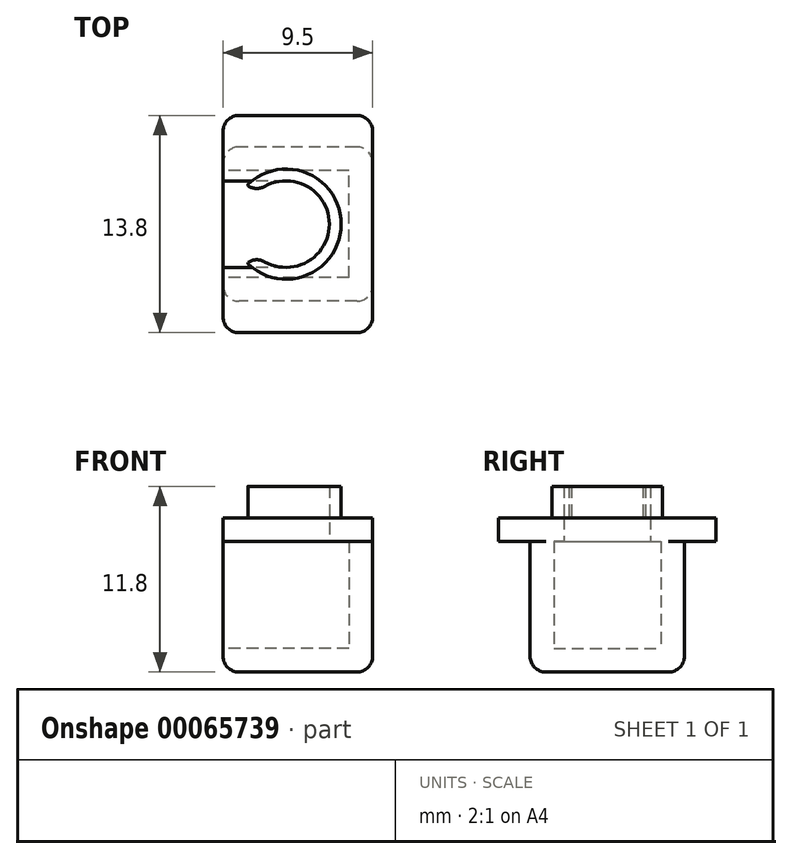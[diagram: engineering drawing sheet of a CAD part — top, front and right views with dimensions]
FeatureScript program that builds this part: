
annotation { "Feature Type Name" : "Feature", "Feature Type Description" : "" }
export const myFeature = defineFeature(function(context is Context, id is Id, definition is map)
    precondition{}
    {
        {
            var Q0;
            Q0=qCreatedBy(makeId("Top.planeOp"),FACE);
            var sketch = newSketch(context, id + "F0", { "sketchPlane" : qUnion([Q0])});
            skLineSegment(sketch, "E0.rect.bottom", {"start": v(4, -3.4) * mm, "end": v(-4, -3.4) * mm});
            skLineSegment(sketch, "E0.rect.top", {"start": v(4, 3.4) * mm, "end": v(-4, 3.4) * mm});
            skLineSegment(sketch, "E0.rect.left", {"start": v(4, -3.4) * mm, "end": v(4, 3.4) * mm});
            skLineSegment(sketch, "E0.rect.right", {"start": v(-4, -3.4) * mm, "end": v(-4, 3.4) * mm});
            skPoint(sketch, "E0.rect.middle", {"position": v(0, 0) * mm});
            skLineSegment(sketch, "E1.0", {"start": v(5.5, 4.9) * mm, "end": v(-4, 4.9) * mm});
            skLineSegment(sketch, "E1.1", {"start": v(5.5, -4.9) * mm, "end": v(5.5, 4.9) * mm});
            skLineSegment(sketch, "E1.2", {"start": v(5.5, -4.9) * mm, "end": v(-4, -4.9) * mm});
            skLineSegment(sketch, "E2", {"start": v(-4, 4.9) * mm, "end": v(-4, 3.4) * mm});
            skLineSegment(sketch, "E3", {"start": v(-4, -3.4) * mm, "end": v(-4, -4.9) * mm});
            skSolve(sketch);
        }
        {
            var Q0;
            Q0 = qSketchRegion(id + "F0", true);
            extrude(context, id + "F1", {"entities" : qUnion([Q0]), "oppositeDirection" : true, "depth" : 1.5 * mm});
        }
        {
            var Q0;
            Q0=makeQuery(id+"F0.imprint","IMPRINT",FACE,{"disambiguationData":[TD([[makeQuery(id+"F0.imprint","IMPRINT",EDGE,{"derivedFrom":sQuery(id+"F0.wireOp",EDGE,"E0.rect.bottom")}),1.0]])]});
            extrude(context, id + "F2", {"entities" : qUnion([Q0]), "operationType" : NewBodyOperationType.ADD, "depth" : 6.8 * mm});
        }
        {
            var Q0;
            Q0=makeQuery(id+"F2.opExtrude","CAP_FACE",FACE,{"disambiguationData":[OSD([sQuery(id+"F0.wireOp",EDGE,"E0.rect.bottom"),sQuery(id+"F0.wireOp",EDGE,"E0.rect.top"),sQuery(id+"F0.wireOp",EDGE,"E0.rect.left"),sQuery(id+"F0.wireOp",EDGE,"E1.0"),sQuery(id+"F0.wireOp",EDGE,"E1.1"),sQuery(id+"F0.wireOp",EDGE,"E1.2"),sQuery(id+"F0.wireOp",EDGE,"E2"),sQuery(id+"F0.wireOp",EDGE,"E3")])],"isStart":false});
            var sketch = newSketch(context, id + "F3", { "sketchPlane" : qUnion([Q0])});
            skArc(sketch, "E4", {"start": v(0, -2.75) * mm, "mid": v(2.75, 0) * mm, "end": v(0, 2.75) * mm});
            skLineSegment(sketch, "E5", {"start": v(0, 2.75) * mm, "end": v(-4, 2.75) * mm});
            skLineSegment(sketch, "E6", {"start": v(-4, 2.75) * mm, "end": v(-4, 4.9) * mm});
            skLineSegment(sketch, "E7", {"start": v(0, -2.75) * mm, "end": v(-4, -2.75) * mm});
            skLineSegment(sketch, "E8", {"start": v(-4, -2.75) * mm, "end": v(-4, -4.9) * mm});
            skSolve(sketch);
        }
        {
            var Q0;
            Q0=makeQuery(id+"F3.imprint","IMPRINT",FACE,{"disambiguationData":[TD([[makeQuery(id+"F3.imprint","IMPRINT",EDGE,{"derivedFrom":sQuery(id+"F3.wireOp",EDGE,"E4")}),-1.0]])]});
            var Q1;
            {var subQ4=makeQuery(id+"F2.opExtrude","CAP_EDGE",EDGE,{"disambiguationData":[OSD([sQuery(id+"F0.wireOp",EDGE,"E0.rect.bottom")])],"isStart":false});Q1=makeQuery(id+"F3.imprint","IMPRINT",FACE,{"disambiguationData":[TD([[makeQuery(id+"F3.imprint","IMPRINT",EDGE,{"derivedFrom":subQ4}),1.0]])]});}
            extrude(context, id + "F4", {"entities" : qUnion([Q0, Q1]), "operationType" : NewBodyOperationType.ADD, "depth" : 1.5 * mm});
        }
        {
            var Q0;
            Q0=makeQuery(id+"F4.opExtrude","CAP_FACE",FACE,{"disambiguationData":[OSD([sQuery(id+"F0.wireOp",EDGE,"E1.0"),sQuery(id+"F0.wireOp",EDGE,"E1.1"),sQuery(id+"F0.wireOp",EDGE,"E1.2"),sQuery(id+"F3.wireOp",EDGE,"E4"),sQuery(id+"F3.wireOp",EDGE,"E5"),sQuery(id+"F3.wireOp",EDGE,"E6"),sQuery(id+"F3.wireOp",EDGE,"E7"),sQuery(id+"F3.wireOp",EDGE,"E8")])],"isStart":false});
            var sketch = newSketch(context, id + "F5", { "sketchPlane" : qUnion([Q0])});
            skArc(sketch, "E9", {"start": v(-1.36, -2.4) * mm, "mid": v(2.75, 0) * mm, "end": v(-1.36, 2.4) * mm});
            skArc(sketch, "E10", {"start": v(-2.38, -2.57) * mm, "mid": v(3.5, 0) * mm, "end": v(-2.38, 2.57) * mm});
            skLineSegment(sketch, "E11", {"start": v(-2.38, 2.38) * mm, "end": v(-2.56, 2.56) * mm});
            skLineSegment(sketch, "E12.MirrorCS", {"start": v(-2.38, -2.38) * mm, "end": v(-2.56, -2.56) * mm});
            skPoint(sketch, "E13.visualSharp", {"position": v(-2.47, 2.47) * mm});
            skArc(sketch, "E13.filletArc", {"start": v(-2.38, 2.57) * mm, "mid": v(-2.42, 2.48) * mm, "end": v(-2.38, 2.38) * mm});
            skPoint(sketch, "E14.visualSharp", {"position": v(-2.47, -2.47) * mm});
            skArc(sketch, "E14.filletArc", {"start": v(-2.38, -2.38) * mm, "mid": v(-2.42, -2.48) * mm, "end": v(-2.38, -2.57) * mm});
            skPoint(sketch, "E15.visualSharp", {"position": v(-1.94, 1.94) * mm});
            skArc(sketch, "E15.filletArc", {"start": v(-2.56, 2.56) * mm, "mid": v(-1.98, 2.27) * mm, "end": v(-1.36, 2.4) * mm});
            skPoint(sketch, "E16.visualSharp", {"position": v(-1.94, -1.94) * mm});
            skArc(sketch, "E16.filletArc", {"start": v(-1.36, -2.4) * mm, "mid": v(-1.98, -2.27) * mm, "end": v(-2.56, -2.56) * mm});
            skSolve(sketch);
        }
        {
            var Q0;
            {var subQ0=sQuery(id+"F5.wireOp",EDGE,"E9");var subQ1=makeQuery(id+"F4.opExtrude","CAP_EDGE",EDGE,{"disambiguationData":[OSD([sQuery(id+"F3.wireOp",EDGE,"E7")])],"isStart":false});var subQ2=makeQuery(id+"F5.imprint","INTERSECT",VERTEX,{"derivedFrom":[subQ1,subQ0]});Q0=makeQuery(id+"F5.imprint","IMPRINT",FACE,{"disambiguationData":[TD([[makeQuery(id+"F5.imprint","IMPRINT",EDGE,{"disambiguationData":[TD([[subQ2,-1.0]])],"derivedFrom":subQ0}),-1.0]])]});}
            var Q1;
            {var subQ1=sQuery(id+"F5.wireOp",EDGE,"E9");var subQ7=makeQuery(id+"F4.opExtrude","CAP_EDGE",EDGE,{"disambiguationData":[OSD([sQuery(id+"F3.wireOp",EDGE,"E5")])],"isStart":false});var subQ9=makeQuery(id+"F5.imprint","INTERSECT",VERTEX,{"derivedFrom":[subQ7,subQ1]});Q1=makeQuery(id+"F5.imprint","IMPRINT",FACE,{"disambiguationData":[TD([[makeQuery(id+"F5.imprint","IMPRINT",EDGE,{"disambiguationData":[TD([[subQ9,-1.0]])],"derivedFrom":subQ1}),-1.0]])]});}
            var Q2;
            {var subQ1=sQuery(id+"F5.wireOp",EDGE,"E9");var subQ7=makeQuery(id+"F4.opExtrude","CAP_EDGE",EDGE,{"disambiguationData":[OSD([sQuery(id+"F3.wireOp",EDGE,"E7")])],"isStart":false});var subQ9=makeQuery(id+"F5.imprint","INTERSECT",VERTEX,{"derivedFrom":[subQ7,subQ1]});Q2=makeQuery(id+"F5.imprint","IMPRINT",FACE,{"disambiguationData":[TD([[makeQuery(id+"F5.imprint","IMPRINT",EDGE,{"disambiguationData":[TD([[subQ9,1.0]])],"derivedFrom":subQ1}),-1.0]])]});}
            extrude(context, id + "F6", {"entities" : qUnion([Q0, Q1, Q2]), "operationType" : NewBodyOperationType.ADD, "depth" : 2 * mm});
        }
        {
            var Q0;
            {var subQ0=sQuery(id+"F0.wireOp",EDGE,"E1.0");Q0=makeQuery(id+"F4.boolean.opBoolean","MERGE",FACE,{"derivedFrom":[makeQuery(id+"F2.boolean.opBoolean","MERGE",FACE,{"derivedFrom":[makeQuery(id+"F1.opExtrude","SWEPT_FACE",FACE,{"disambiguationData":[OSD([subQ0])]}),makeQuery(id+"F2.opExtrude","SWEPT_FACE",FACE,{"disambiguationData":[OSD([subQ0])]})]}),makeQuery(id+"F4.opExtrude","SWEPT_FACE",FACE,{"disambiguationData":[OSD([subQ0])]})]});}
            var sketch = newSketch(context, id + "F7", { "sketchPlane" : qUnion([Q0])});
            skLineSegment(sketch, "E17", {"start": v(-5.5, 6.8) * mm, "end": v(4, 6.8) * mm});
            skSolve(sketch);
        }
        {
            var Q0;
            {var subQ0=sQuery(id+"F7.wireOp",EDGE,"E17");Q0=makeQuery(id+"F7.imprint","IMPRINT",FACE,{"disambiguationData":[TD([[makeQuery(id+"F7.imprint","IMPRINT",EDGE,{"derivedFrom":subQ0}),1.0]])]});}
            extrude(context, id + "F8", {"entities" : qUnion([Q0]), "operationType" : NewBodyOperationType.ADD, "depth" : 2 * mm});
        }
        {
            var Q0;
            {var subQ0=sQuery(id+"F0.wireOp",EDGE,"E1.2");Q0=makeQuery(id+"F4.boolean.opBoolean","MERGE",FACE,{"derivedFrom":[makeQuery(id+"F2.boolean.opBoolean","MERGE",FACE,{"derivedFrom":[makeQuery(id+"F1.opExtrude","SWEPT_FACE",FACE,{"disambiguationData":[OSD([subQ0])]}),makeQuery(id+"F2.opExtrude","SWEPT_FACE",FACE,{"disambiguationData":[OSD([subQ0])]})]}),makeQuery(id+"F4.opExtrude","SWEPT_FACE",FACE,{"disambiguationData":[OSD([subQ0])]})]});}
            var sketch = newSketch(context, id + "F9", { "sketchPlane" : qUnion([Q0])});
            skLineSegment(sketch, "E18", {"start": v(5.5, 6.8) * mm, "end": v(-4, 6.8) * mm});
            skSolve(sketch);
        }
        {
            var Q0;
            {var subQ0=sQuery(id+"F9.wireOp",EDGE,"E18");Q0=makeQuery(id+"F9.imprint","IMPRINT",FACE,{"disambiguationData":[TD([[makeQuery(id+"F9.imprint","IMPRINT",EDGE,{"derivedFrom":subQ0}),-1.0]])]});}
            extrude(context, id + "F10", {"entities" : qUnion([Q0]), "operationType" : NewBodyOperationType.ADD, "depth" : 2 * mm});
        }
        {
            var Q0;
            Q0=makeQuery(id+"F1.opExtrude","CAP_EDGE",EDGE,{"disambiguationData":[OSD([sQuery(id+"F0.wireOp",EDGE,"E1.2")])],"isStart":false});
            var Q1;
            {var subQ0=sQuery(id+"F0.wireOp",EDGE,"E1.2");var subQ1=sQuery(id+"F0.wireOp",EDGE,"E1.1");Q1=makeQuery(id+"F4.boolean.opBoolean","MERGE",EDGE,{"derivedFrom":[makeQuery(id+"F2.boolean.opBoolean","MERGE",EDGE,{"derivedFrom":[makeQuery(id+"F1.opExtrude","SWEPT_EDGE",EDGE,{"disambiguationData":[OSD([subQ1,subQ0])]}),makeQuery(id+"F2.opExtrude","SWEPT_EDGE",EDGE,{"disambiguationData":[OSD([subQ1,subQ0])]})]}),makeQuery(id+"F4.opExtrude","SWEPT_EDGE",EDGE,{"disambiguationData":[OSD([subQ1,subQ0])]})]});}
            var Q2;
            {var subQ0=sQuery(id+"F0.wireOp",EDGE,"E1.1");var subQ1=sQuery(id+"F0.wireOp",EDGE,"E1.0");Q2=makeQuery(id+"F4.boolean.opBoolean","MERGE",EDGE,{"derivedFrom":[makeQuery(id+"F2.boolean.opBoolean","MERGE",EDGE,{"derivedFrom":[makeQuery(id+"F1.opExtrude","SWEPT_EDGE",EDGE,{"disambiguationData":[OSD([subQ1,subQ0])]}),makeQuery(id+"F2.opExtrude","SWEPT_EDGE",EDGE,{"disambiguationData":[OSD([subQ1,subQ0])]})]}),makeQuery(id+"F4.opExtrude","SWEPT_EDGE",EDGE,{"disambiguationData":[OSD([subQ1,subQ0])]})]});}
            var Q3;
            Q3=makeQuery(id+"F1.opExtrude","CAP_EDGE",EDGE,{"disambiguationData":[OSD([sQuery(id+"F0.wireOp",EDGE,"E1.1")])],"isStart":false});
            var Q4;
            Q4=makeQuery(id+"F1.opExtrude","CAP_EDGE",EDGE,{"disambiguationData":[OSD([sQuery(id+"F0.wireOp",EDGE,"E1.0")])],"isStart":false});
            var Q5;
            {var subQ0=sQuery(id+"F0.wireOp",EDGE,"E1.0");var subQ1=sQuery(id+"F0.wireOp",EDGE,"E2");Q5=makeQuery(id+"F4.boolean.opBoolean","MERGE",EDGE,{"derivedFrom":[makeQuery(id+"F2.boolean.opBoolean","MERGE",EDGE,{"derivedFrom":[makeQuery(id+"F1.opExtrude","SWEPT_EDGE",EDGE,{"disambiguationData":[OSD([subQ0,subQ1])]}),makeQuery(id+"F2.opExtrude","SWEPT_EDGE",EDGE,{"disambiguationData":[OSD([subQ0,subQ1])]})]}),makeQuery(id+"F4.opExtrude","SWEPT_EDGE",EDGE,{"disambiguationData":[OSD([subQ0,sQuery(id+"F3.wireOp",EDGE,"E6")])]})]});}
            var Q6;
            Q6=makeQuery(id+"F1.opExtrude","CAP_EDGE",EDGE,{"disambiguationData":[OSD([sQuery(id+"F0.wireOp",EDGE,"E0.rect.right"),sQuery(id+"F0.wireOp",EDGE,"E2"),sQuery(id+"F0.wireOp",EDGE,"E3")])],"isStart":false});
            var Q7;
            {var subQ0=sQuery(id+"F0.wireOp",EDGE,"E1.2");var subQ1=sQuery(id+"F0.wireOp",EDGE,"E3");Q7=makeQuery(id+"F4.boolean.opBoolean","MERGE",EDGE,{"derivedFrom":[makeQuery(id+"F2.boolean.opBoolean","MERGE",EDGE,{"derivedFrom":[makeQuery(id+"F1.opExtrude","SWEPT_EDGE",EDGE,{"disambiguationData":[OSD([subQ0,subQ1])]}),makeQuery(id+"F2.opExtrude","SWEPT_EDGE",EDGE,{"disambiguationData":[OSD([subQ0,subQ1])]})]}),makeQuery(id+"F4.opExtrude","SWEPT_EDGE",EDGE,{"disambiguationData":[OSD([subQ0,sQuery(id+"F3.wireOp",EDGE,"E8")])]})]});}
            var Q8;
            Q8=makeQuery(id+"F10.opExtrude","CAP_EDGE",EDGE,{"disambiguationData":[OSD([sQuery(id+"F9.wireOp",EDGE,"E18")])],"isStart":true});
            var Q9;
            Q9=makeQuery(id+"F8.opExtrude","CAP_EDGE",EDGE,{"disambiguationData":[OSD([sQuery(id+"F7.wireOp",EDGE,"E17")])],"isStart":true});
            var Q10;
            Q10=makeQuery(id+"F8.opExtrude","CAP_EDGE",EDGE,{"disambiguationData":[OSD([sQuery(id+"F0.wireOp",EDGE,"E1.0"),sQuery(id+"F0.wireOp",EDGE,"E2"),sQuery(id+"F3.wireOp",EDGE,"E6")])],"isStart":false});
            var Q11;
            Q11=makeQuery(id+"F8.opExtrude","CAP_EDGE",EDGE,{"disambiguationData":[OSD([sQuery(id+"F0.wireOp",EDGE,"E1.0"),sQuery(id+"F0.wireOp",EDGE,"E1.1")])],"isStart":false});
            var Q12;
            Q12=makeQuery(id+"F10.opExtrude","CAP_EDGE",EDGE,{"disambiguationData":[OSD([sQuery(id+"F0.wireOp",EDGE,"E1.1"),sQuery(id+"F0.wireOp",EDGE,"E1.2")])],"isStart":false});
            var Q13;
            Q13=makeQuery(id+"F10.opExtrude","CAP_EDGE",EDGE,{"disambiguationData":[OSD([sQuery(id+"F0.wireOp",EDGE,"E1.2"),sQuery(id+"F0.wireOp",EDGE,"E3"),sQuery(id+"F3.wireOp",EDGE,"E8")])],"isStart":false});
            fillet(context, id + "F11", {"entities" : qUnion([Q0, Q1, Q2, Q3, Q4, Q5, Q6, Q7, Q8, Q9, Q10, Q11, Q12, Q13]), "radius" : 1 * mm, "tangentPropagation" : true, "allowEdgeOverflow" : false});
        }
    });
